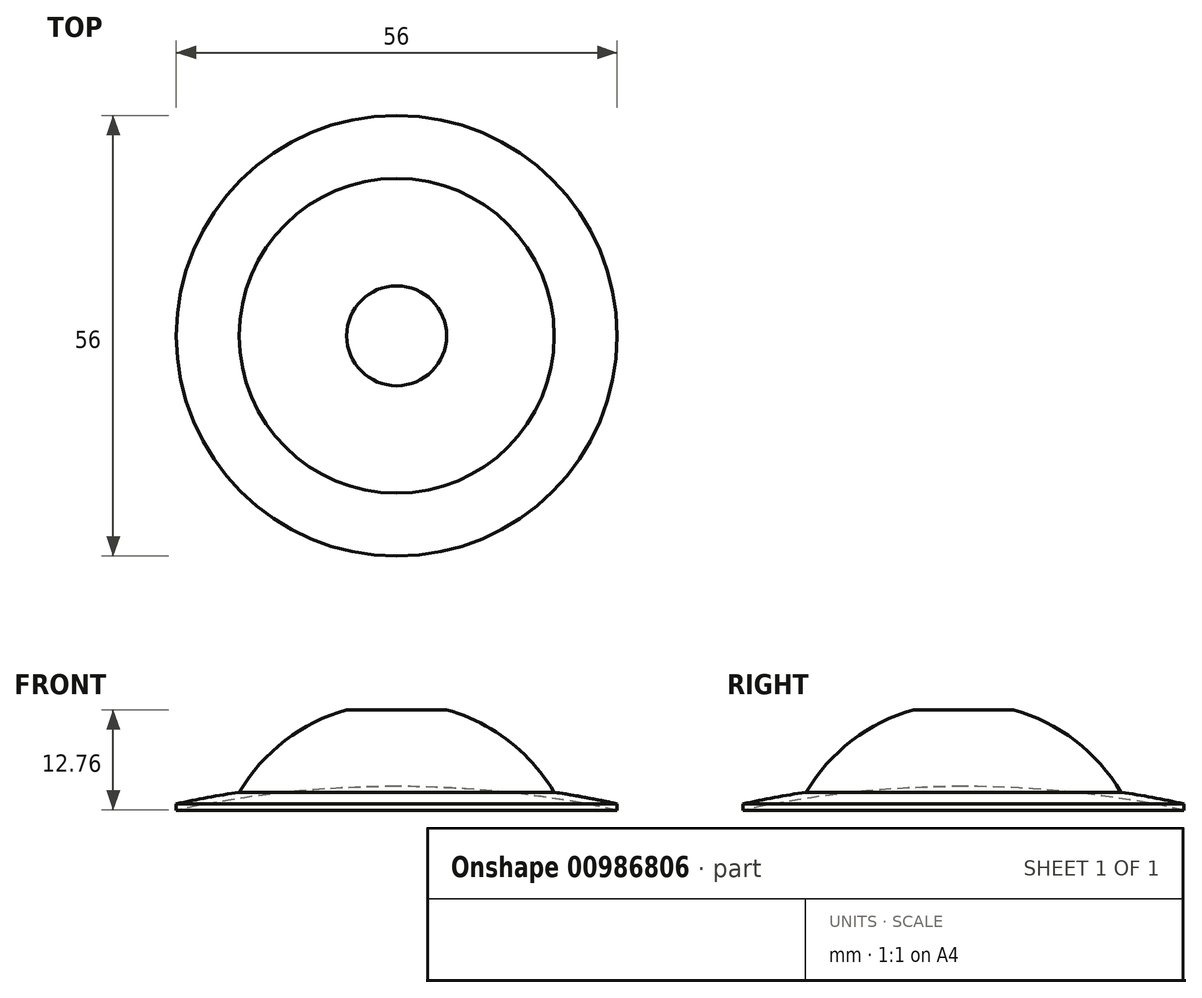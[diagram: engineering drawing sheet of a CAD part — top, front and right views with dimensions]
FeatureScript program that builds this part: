
annotation { "Feature Type Name" : "Feature", "Feature Type Description" : "" }
export const myFeature = defineFeature(function(context is Context, id is Id, definition is map)
    precondition{}
    {
        {
            var Q0;
            Q0=qCreatedBy(makeId("Front.planeOp"),FACE);
            var sketch = newSketch(context, id + "F0", { "sketchPlane" : qUnion([Q0])});
            skArc(sketch, "E0", {"start": v(-20, -4.1) * mm, "mid": v(-24.01, -4.78) * mm, "end": v(-28, -5.58) * mm});
            skLineSegment(sketch, "E1", {"start": v(-6.35, 6.38) * mm, "end": v(0, 6.38) * mm});
            skLineSegment(sketch, "E2", {"start": v(-28, -5.58) * mm, "end": v(-28, -6.38) * mm});
            skArc(sketch, "E3", {"start": v(0, -3.38) * mm, "mid": v(-14.08, -4.13) * mm, "end": v(-28, -6.38) * mm});
            skArc(sketch, "E4", {"start": v(-6.35, 6.38) * mm, "mid": v(-14.18, 2.45) * mm, "end": v(-20, -4.1) * mm});
            skLineSegment(sketch, "E5", {"start": v(0, 6.38) * mm, "end": v(0, -3.38) * mm});
            skSolve(sketch);
        }
        {
            var Q0;
            Q0 = qSketchRegion(id + "F0", true);
            var Q1;
            Q1=sQuery(id+"F0.wireOp",EDGE,"E5");
            revolve(context, id + "F1", {"surfaceOperationType" : NewSurfaceOperationType.NEW, "entities" : qUnion([Q0]), "axis" : qUnion([Q1]), "revolveType" : RevolveType.FULL});
        }
    });
